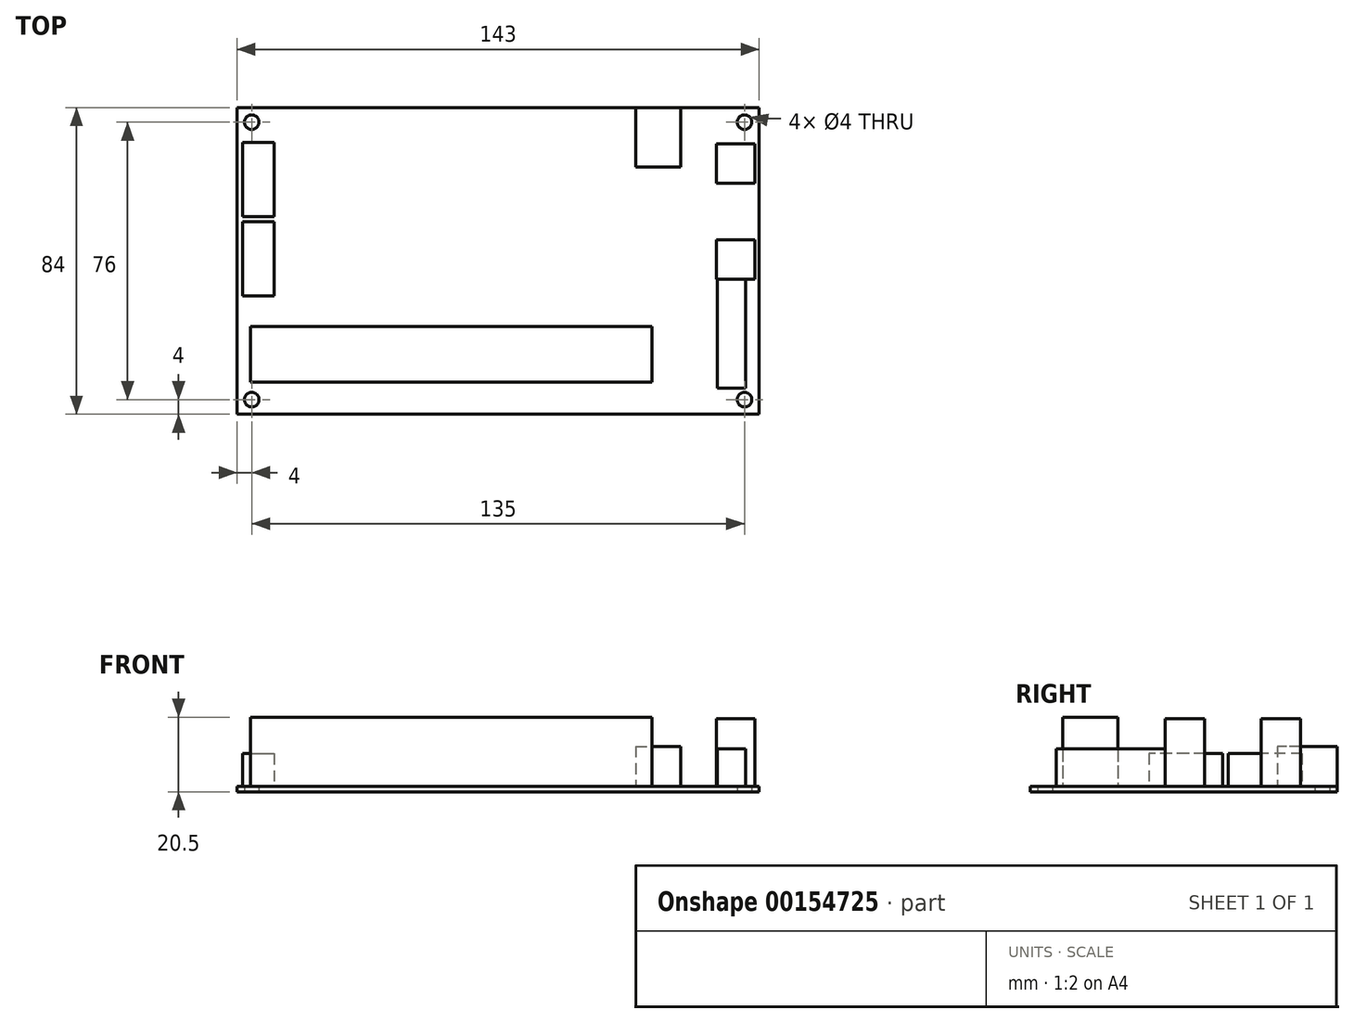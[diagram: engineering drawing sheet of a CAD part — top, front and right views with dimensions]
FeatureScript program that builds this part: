
annotation { "Feature Type Name" : "Feature", "Feature Type Description" : "" }
export const myFeature = defineFeature(function(context is Context, id is Id, definition is map)
    precondition{}
    {
        {
            var Q0;
            Q0=qCreatedBy(makeId("Top.planeOp"),FACE);
            var sketch = newSketch(context, id + "F0", { "sketchPlane" : qUnion([Q0])});
            skLineSegment(sketch, "E0.bottom", {"start": v(0, 84) * mm, "end": v(143, 84) * mm});
            skLineSegment(sketch, "E0.top", {"start": v(0, 0) * mm, "end": v(143, 0) * mm});
            skLineSegment(sketch, "E0.left", {"start": v(0, 84) * mm, "end": v(0, 0) * mm});
            skLineSegment(sketch, "E0.right", {"start": v(143, 84) * mm, "end": v(143, 0) * mm});
            skSolve(sketch);
        }
        {
            var Q0;
            Q0 = qSketchRegion(id + "F0", true);
            extrude(context, id + "F1", {"entities" : qUnion([Q0]), "depth" : 1.5 * mm});
        }
        {
            var Q0;
            Q0=makeQuery(id+"F1.opExtrude","CAP_FACE",FACE,{"disambiguationData":[OSD([sQuery(id+"F0.wireOp",EDGE,"E0.bottom"),sQuery(id+"F0.wireOp",EDGE,"E0.top"),sQuery(id+"F0.wireOp",EDGE,"E0.left"),sQuery(id+"F0.wireOp",EDGE,"E0.right")])],"isStart":false});
            var sketch = newSketch(context, id + "F2", { "sketchPlane" : qUnion([Q0])});
            skCircle(sketch, "E1", {"center": v(139, 4) * mm, "radius": 2 * mm});
            skLineSegment(sketch, "E2", {"start": v(71.5, 84) * mm, "end": v(71.5, 0) * mm, "construction": true});
            skLineSegment(sketch, "E3", {"start": v(0, 42) * mm, "end": v(143, 42) * mm, "construction": true});
            skCircle(sketch, "E4.MirrorC", {"center": v(139, 80) * mm, "radius": 2 * mm});
            skLineSegment(sketch, "E5.MirrorCS", {"start": v(71.5, 0) * mm, "end": v(71.5, 84) * mm, "construction": true});
            skCircle(sketch, "E6.MirrorC", {"center": v(4, 80) * mm, "radius": 2 * mm});
            skCircle(sketch, "E7.MirrorC", {"center": v(4, 4) * mm, "radius": 2 * mm});
            skSolve(sketch);
        }
        {
            var Q0;
            Q0 = qSketchRegion(id + "F2", true);
            extrude(context, id + "F3", {"entities" : qUnion([Q0]), "operationType" : NewBodyOperationType.REMOVE, "endBound" : BoundingType.SYMMETRIC, "depth" : 25 * mm});
        }
        {
            var Q0;
            Q0=makeQuery(id+"F1.opExtrude","CAP_FACE",FACE,{"disambiguationData":[OSD([sQuery(id+"F0.wireOp",EDGE,"E0.bottom"),sQuery(id+"F0.wireOp",EDGE,"E0.top"),sQuery(id+"F0.wireOp",EDGE,"E0.left"),sQuery(id+"F0.wireOp",EDGE,"E0.right")])],"isStart":false});
            var sketch = newSketch(context, id + "F4", { "sketchPlane" : qUnion([Q0])});
            skLineSegment(sketch, "E8.bottom", {"start": v(131.36, 74) * mm, "end": v(141.8, 74) * mm});
            skLineSegment(sketch, "E8.top", {"start": v(131.36, 63.24) * mm, "end": v(141.8, 63.24) * mm});
            skLineSegment(sketch, "E8.left", {"start": v(131.36, 74) * mm, "end": v(131.36, 63.24) * mm});
            skLineSegment(sketch, "E8.right", {"start": v(141.8, 74) * mm, "end": v(141.8, 63.24) * mm});
            skLineSegment(sketch, "E9.bottom", {"start": v(131.36, 47.74) * mm, "end": v(141.8, 47.74) * mm});
            skLineSegment(sketch, "E9.top", {"start": v(131.36, 36.98) * mm, "end": v(141.8, 36.98) * mm});
            skLineSegment(sketch, "E9.left", {"start": v(131.36, 47.74) * mm, "end": v(131.36, 36.98) * mm});
            skLineSegment(sketch, "E9.right", {"start": v(141.8, 47.74) * mm, "end": v(141.8, 36.98) * mm});
            skSolve(sketch);
        }
        {
            var Q0;
            Q0 = qSketchRegion(id + "F4", true);
            extrude(context, id + "F5", {"entities" : qUnion([Q0]), "operationType" : NewBodyOperationType.ADD, "depth" : 18.62 * mm});
        }
        {
            var Q0;
            Q0=makeQuery(id+"F1.opExtrude","CAP_FACE",FACE,{"disambiguationData":[OSD([sQuery(id+"F0.wireOp",EDGE,"E0.bottom"),sQuery(id+"F0.wireOp",EDGE,"E0.top"),sQuery(id+"F0.wireOp",EDGE,"E0.left"),sQuery(id+"F0.wireOp",EDGE,"E0.right")])],"isStart":false});
            var sketch = newSketch(context, id + "F6", { "sketchPlane" : qUnion([Q0])});
            skLineSegment(sketch, "E10.bottom", {"start": v(131.5, 37.13) * mm, "end": v(139.3, 37.13) * mm});
            skLineSegment(sketch, "E10.top", {"start": v(131.5, 7.13) * mm, "end": v(139.3, 7.13) * mm});
            skLineSegment(sketch, "E10.left", {"start": v(131.5, 37.13) * mm, "end": v(131.5, 7.13) * mm});
            skLineSegment(sketch, "E10.right", {"start": v(139.3, 37.13) * mm, "end": v(139.3, 7.13) * mm});
            skSolve(sketch);
        }
        {
            var Q0;
            Q0 = qSketchRegion(id + "F6", true);
            extrude(context, id + "F7", {"entities" : qUnion([Q0]), "operationType" : NewBodyOperationType.ADD, "depth" : 10.3 * mm});
        }
        {
            var Q0;
            Q0=makeQuery(id+"F1.opExtrude","CAP_FACE",FACE,{"disambiguationData":[OSD([sQuery(id+"F0.wireOp",EDGE,"E0.bottom"),sQuery(id+"F0.wireOp",EDGE,"E0.top"),sQuery(id+"F0.wireOp",EDGE,"E0.left"),sQuery(id+"F0.wireOp",EDGE,"E0.right")])],"isStart":false});
            var sketch = newSketch(context, id + "F8", { "sketchPlane" : qUnion([Q0])});
            skLineSegment(sketch, "E11.bottom", {"start": v(1.5, 74.43) * mm, "end": v(10.2, 74.43) * mm});
            skLineSegment(sketch, "E11.top", {"start": v(1.5, 54.18) * mm, "end": v(10.2, 54.18) * mm});
            skLineSegment(sketch, "E11.left", {"start": v(1.5, 74.43) * mm, "end": v(1.5, 54.18) * mm});
            skLineSegment(sketch, "E11.right", {"start": v(10.2, 74.43) * mm, "end": v(10.2, 54.18) * mm});
            skLineSegment(sketch, "E12.bottom", {"start": v(1.5, 52.68) * mm, "end": v(10.2, 52.68) * mm});
            skLineSegment(sketch, "E12.top", {"start": v(1.5, 32.43) * mm, "end": v(10.2, 32.43) * mm});
            skLineSegment(sketch, "E12.left", {"start": v(1.5, 52.68) * mm, "end": v(1.5, 32.43) * mm});
            skLineSegment(sketch, "E12.right", {"start": v(10.2, 52.68) * mm, "end": v(10.2, 32.43) * mm});
            skLineSegment(sketch, "E13", {"start": v(1.5, 70.08) * mm, "end": v(1.5, 18.36) * mm, "construction": true});
            skSolve(sketch);
        }
        {
            var Q0;
            Q0 = qSketchRegion(id + "F8", true);
            extrude(context, id + "F9", {"entities" : qUnion([Q0]), "operationType" : NewBodyOperationType.ADD, "depth" : 9 * mm});
        }
        {
            var Q0;
            Q0=makeQuery(id+"F1.opExtrude","CAP_FACE",FACE,{"disambiguationData":[OSD([sQuery(id+"F0.wireOp",EDGE,"E0.bottom"),sQuery(id+"F0.wireOp",EDGE,"E0.top"),sQuery(id+"F0.wireOp",EDGE,"E0.left"),sQuery(id+"F0.wireOp",EDGE,"E0.right")])],"isStart":false});
            var sketch = newSketch(context, id + "F10", { "sketchPlane" : qUnion([Q0])});
            skLineSegment(sketch, "E14.bottom", {"start": v(3.7, 24) * mm, "end": v(113.7, 24) * mm});
            skLineSegment(sketch, "E14.top", {"start": v(3.7, 8.8) * mm, "end": v(113.7, 8.8) * mm});
            skLineSegment(sketch, "E14.left", {"start": v(3.7, 24) * mm, "end": v(3.7, 8.8) * mm});
            skLineSegment(sketch, "E14.right", {"start": v(113.7, 24) * mm, "end": v(113.7, 8.8) * mm});
            skSolve(sketch);
        }
        {
            var Q0;
            Q0 = qSketchRegion(id + "F10", true);
            extrude(context, id + "F11", {"entities" : qUnion([Q0]), "operationType" : NewBodyOperationType.ADD, "depth" : 19 * mm});
        }
        {
            var Q0;
            Q0=makeQuery(id+"F1.opExtrude","CAP_FACE",FACE,{"disambiguationData":[OSD([sQuery(id+"F0.wireOp",EDGE,"E0.bottom"),sQuery(id+"F0.wireOp",EDGE,"E0.top"),sQuery(id+"F0.wireOp",EDGE,"E0.left"),sQuery(id+"F0.wireOp",EDGE,"E0.right")])],"isStart":false});
            var sketch = newSketch(context, id + "F12", { "sketchPlane" : qUnion([Q0])});
            skLineSegment(sketch, "E15.bottom", {"start": v(109.2, 84) * mm, "end": v(121.5, 84) * mm});
            skLineSegment(sketch, "E15.top", {"start": v(109.2, 67.7) * mm, "end": v(121.5, 67.7) * mm});
            skLineSegment(sketch, "E15.left", {"start": v(121.5, 84) * mm, "end": v(121.5, 67.7) * mm});
            skLineSegment(sketch, "E15.right", {"start": v(109.2, 84) * mm, "end": v(109.2, 67.7) * mm});
            skSolve(sketch);
        }
        {
            var Q0;
            Q0 = qSketchRegion(id + "F12", true);
            extrude(context, id + "F13", {"entities" : qUnion([Q0]), "operationType" : NewBodyOperationType.ADD, "depth" : 11 * mm});
        }
    });
